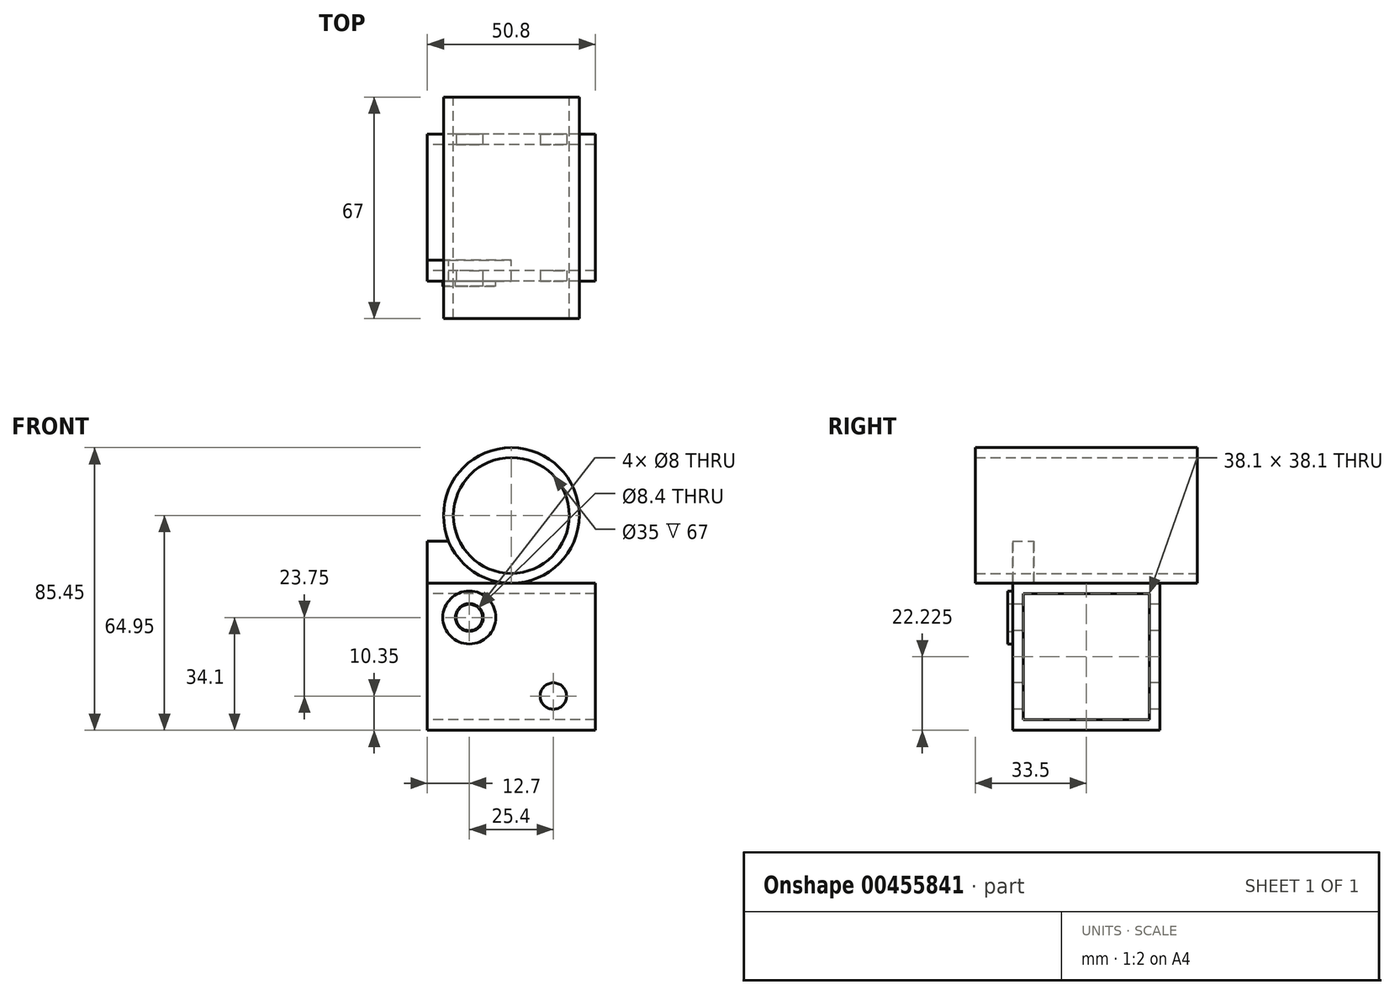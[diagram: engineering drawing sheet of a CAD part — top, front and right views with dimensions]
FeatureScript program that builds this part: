
annotation { "Feature Type Name" : "Feature", "Feature Type Description" : "" }
export const myFeature = defineFeature(function(context is Context, id is Id, definition is map)
    precondition{}
    {
        {
            var Q0;
            Q0=qCreatedBy(makeId("Front.planeOp"),FACE);
            var sketch = newSketch(context, id + "F0", { "sketchPlane" : qUnion([Q0])});
            skCircle(sketch, "E0", {"center": v(0, 0) * mm, "radius": 20.5 * mm});
            skCircle(sketch, "E1", {"center": v(0, 0) * mm, "radius": 17.5 * mm});
            skSolve(sketch);
        }
        {
            var Q0;
            Q0 = qSketchRegion(id + "F0", true);
            extrude(context, id + "F1", {"entities" : qUnion([Q0]), "depth" : 67 * mm, "offsetDistance" : 25.4 * mm, "symmetric" : true});
        }
        {
            var Q0;
            Q0=qCreatedBy(makeId("Right.planeOp"),FACE);
            var sketch = newSketch(context, id + "F2", { "sketchPlane" : qUnion([Q0])});
            skLineSegment(sketch, "E2.bottom", {"start": v(22.23, -20.5) * mm, "end": v(-22.23, -20.5) * mm});
            skLineSegment(sketch, "E2.top", {"start": v(22.22, -64.95) * mm, "end": v(-22.23, -64.95) * mm});
            skLineSegment(sketch, "E2.left", {"start": v(22.23, -20.5) * mm, "end": v(22.22, -64.95) * mm});
            skLineSegment(sketch, "E2.right", {"start": v(-22.23, -20.5) * mm, "end": v(-22.23, -64.95) * mm});
            skPoint(sketch, "E2.middle", {"position": v(0, -42.73) * mm});
            skLineSegment(sketch, "E3.bottom", {"start": v(19.05, -23.68) * mm, "end": v(-19.05, -23.68) * mm});
            skLineSegment(sketch, "E3.top", {"start": v(19.05, -61.78) * mm, "end": v(-19.05, -61.78) * mm});
            skLineSegment(sketch, "E3.left", {"start": v(19.05, -23.67) * mm, "end": v(19.05, -61.78) * mm});
            skLineSegment(sketch, "E3.right", {"start": v(-19.05, -23.68) * mm, "end": v(-19.05, -61.78) * mm});
            skSolve(sketch);
        }
        {
            var Q0;
            Q0=makeQuery(id+"F2.imprint","IMPRINT",FACE,{"disambiguationData":[TD([[makeQuery(id+"F2.imprint","IMPRINT",EDGE,{"derivedFrom":sQuery(id+"F2.wireOp",EDGE,"E2.bottom")}),1.0]])]});
            extrude(context, id + "F3", {"entities" : qUnion([Q0]), "depth" : 25.4 * mm, "offsetDistance" : 25.4 * mm, "hasSecondDirection" : true, "secondDirectionOppositeDirection" : true, "secondDirectionDepth" : 25.4 * mm});
        }
        {
            var Q0;
            Q0=makeQuery(id+"F3.opExtrude","SWEPT_FACE",FACE,{"disambiguationData":[OSD([sQuery(id+"F2.wireOp",EDGE,"E2.right")])]});
            var sketch = newSketch(context, id + "F4", { "sketchPlane" : qUnion([Q0])});
            skCircle(sketch, "E4", {"center": v(-12.7, -30.85) * mm, "radius": 4 * mm});
            skCircle(sketch, "E5", {"center": v(12.7, -54.6) * mm, "radius": 4 * mm});
            skLineSegment(sketch, "E6", {"start": v(-25.4, -42.73) * mm, "end": v(25.4, -42.73) * mm, "construction": true});
            skLineSegment(sketch, "E7", {"start": v(-25.4, -26.85) * mm, "end": v(-8.5, -26.85) * mm, "construction": true});
            skLineSegment(sketch, "E8", {"start": v(25.4, -58.6) * mm, "end": v(3.44, -58.6) * mm, "construction": true});
            skSolve(sketch);
        }
        {
            var Q0;
            Q0 = qSketchRegion(id + "F4", true);
            extrude(context, id + "F5", {"entities" : qUnion([Q0]), "operationType" : NewBodyOperationType.REMOVE, "endBound" : BoundingType.THROUGH_ALL, "oppositeDirection" : true, "depth" : 25.4 * mm, "offsetDistance" : 25.4 * mm});
        }
        {
            var Q0;
            Q0=qCreatedBy(makeId("Front.planeOp"),FACE);
            var sketch = newSketch(context, id + "F6", { "sketchPlane" : qUnion([Q0])});
            skLineSegment(sketch, "E9.0", {"start": v(25.4, -20.5) * mm, "end": v(-25.4, -20.5) * mm});
            skCircle(sketch, "E10.0", {"center": v(0, 0) * mm, "radius": 20.5 * mm});
            skLineSegment(sketch, "E11", {"start": v(-25.4, -20.5) * mm, "end": v(-25.4, -7.8) * mm});
            skLineSegment(sketch, "E12", {"start": v(-25.4, -7.8) * mm, "end": v(-18.96, -7.8) * mm});
            skSolve(sketch);
        }
        {
            var Q0;
            {var subQ0=sQuery(id+"F6.wireOp",EDGE,"E11");Q0=makeQuery(id+"F6.imprint","IMPRINT",FACE,{"disambiguationData":[TD([[makeQuery(id+"F6.imprint","IMPRINT",EDGE,{"derivedFrom":subQ0}),-1.0]])]});}
            extrude(context, id + "F7", {"entities" : qUnion([Q0]), "depth" : 22.22 * mm, "offsetDistance" : 25.4 * mm, "hasSecondDirection" : true, "secondDirectionOppositeDirection" : false, "secondDirectionDepth" : 15.88 * mm});
        }
        {
            var Q0;
            Q0=makeQuery(id+"F3.opExtrude","SWEPT_FACE",FACE,{"disambiguationData":[OSD([sQuery(id+"F2.wireOp",EDGE,"E2.right")])]});
            var sketch = newSketch(context, id + "F8", { "sketchPlane" : qUnion([Q0])});
            skCircle(sketch, "E13", {"center": v(-12.7, -30.85) * mm, "radius": 4.2 * mm});
            skCircle(sketch, "E14", {"center": v(-12.7, -30.85) * mm, "radius": 8 * mm});
            skSolve(sketch);
        }
        {
            var Q0;
            Q0 = qSketchRegion(id + "F8", true);
            extrude(context, id + "F9", {"entities" : qUnion([Q0]), "depth" : 1.5 * mm, "offsetDistance" : 25.4 * mm});
        }
    });
